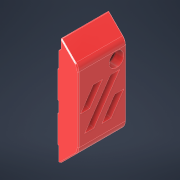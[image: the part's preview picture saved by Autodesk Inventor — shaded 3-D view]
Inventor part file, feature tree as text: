
AUTODESK INVENTOR PART (.ipt)
format: ipt  version: 2022.1 (Build 261234000, 234)  size: 578,560 bytes
history: native  units: mm
features: extrude x9, sketch x8, chamfer x7, projected_geometry x6, plane x3, reference x3, other x3, direct_edit x2, fillet x2, move_body x2, delete_face x1, hole x1
ambient origin geometry x8: Origin, YZ Plane, XZ Plane, XY Plane, X Axis, Y Axis, Z Axis, Center Point
bodies: Volumenkörper1 (feature_tree)
feature tree (47):
  extrude  "Extrusion1"  Depth=6.4mm
  plane  "Arbeitsebene1"
  extrude  "Extrusion2"  Depth=6.4mm
  chamfer  "Fase1"  Distance=6.4mm
  extrude  "Extrusion3"  Depth=10.0mm
  direct_edit  "Direktbearbeitung1"
  plane  "Arbeitsebene3"
  extrude  "Extrusion4"  Depth=10.0mm
  plane  "Arbeitsebene2"
  extrude  "Extrusion5"  Depth=10.0mm
  delete_face  "Fläche löschen1"
  extrude  "Extrusion7"  Depth=10.0mm TaperAngle=0.0deg
  extrude  "Extrusion8"  Depth=10.0mm
  chamfer  "Fase5"  Distance=7.9mm
  chamfer  "Fase6"  Distance=7.0mm Angle=45.0deg
  extrude  "Extrusion11"  TaperAngle=45.0deg  [1 undecoded]
  sketch  "Skizze13"  dims[d9=6.4mm d10=6.4mm d11=5.0mm d12=5.0mm d13=0.1mm d14=0.4mm d15=0.0mm d16=0.1mm d17=7.9mm d18=0.0mm d19=7.0mm d20=2.0mm d21=45.0deg d22=45.0deg d23=0.05mm d24=45.0deg d25=0.05mm d26=0.4mm d27=8.0mm d28=0.0mm d29=0.0mm d30=0.0mm d31=0.2mm d97=25.438174mm d99=3.8mm d102=3.304348mm d103=9.5mm d104=19.0mm d106=0.0mm d110=3.8mm d111=19.0mm d113=3.8mm d114=9.5mm d118=0.0mm d119=3.304348mm d124=15.705205mm d125=18.008696mm d126=25.215728mm d127=20.0mm d129=0.995652mm d130=1.0mm d131=0.0mm d146=20.0mm d147=10.0mm d148=12.607864mm d149=5.6mm d153=6.1mm d154=7.397555mm d155=2.198777mm d156=4.05mm d157=3.5mm d158=0.0mm d159=2.0mm d167=0.0mm d168=0.4mm d169=0.0mm d170=0.0mm d172=0.01mm d173=0.05mm d175=0.05mm d176=4.95mm d177=0.0mm d178=1.99mm d179=2.0mm d180=45.0deg d200=1.0mm d201=2.0mm d202=45.0deg d203=0.0mm d204=0.0mm d205=0.42mm d206=0.0mm d207=0.4mm d208=0.1mm d209=20.0mm d210=0.42mm d211=2.0mm d212=45.0deg d213=6.1mm d214=6.0mm d215=4.0mm d216=2.0mm d217=90.0deg d218=3.2mm d219=0.0mm d220=0.2mm d221=2.0mm d222=45.0deg d226=0.2mm d227=2.0mm d228=45.0deg d229=4.0mm d233=0.4mm d234=2.0mm d235=45.0deg d236=0.0mm d237=0.0mm d238=-0.5mm d171=0.872665mm]
  extrude  "Extrusion12"  Depth=10.0mm
  fillet  "Rundung7"  [1 undecoded]
  chamfer  "Fase7"  Distance=0.05mm
  hole  "Bohrung2"  [1 undecoded]
  chamfer  "Fase8"  Distance=8.0mm
  chamfer  "Fase10"  Distance=0.2mm
  fillet  "Rundung8"  Radius=25.438174mm
  chamfer  "Fase12"  Distance=3.8mm
  direct_edit  "Direktbearbeitung2"
  sketch  "Skizze1"  dims[d0=3.25mm d1=6.4mm]
  reference  "Referenz1"
  sketch  "Skizze2"  dims[d2=6.4mm d3=6.4mm]
  reference  "Referenz2"
  sketch  "Skizze3"  dims[d4=6.4mm]
  projected_geometry  "Projizierte Kontur1"
  sketch  "Skizze6"  dims[d5=6.4mm]
  sketch  "Skizze8"  dims[d6=5.0mm]
  reference  "Referenz13"
  sketch  "Skizze9"  dims[d7=5.0mm]
  sketch  "Skizze12"  dims[d8=6.4mm]
  projected_geometry  "Projizierte Kontur3"
  projected_geometry  "Projizierte Kontur4"
  projected_geometry  "Projizierte Kontur5"
  projected_geometry  "Projizierte Kontur6"
  projected_geometry  "Projizierte Kontur7"
  other  "<userpath>\Desktop\Voron-2-2.4r1\Custom\Misumi GE5C\Gruppe.iam"
  other  "Gruppe.iam"
  other  "Z-Joint-Normal:1"
  move_body  "Verschieben1"
  move_body  "Verschieben2"
note: 3 required parameter values undecoded (feature->parameter linkage not recoverable at this tier; creation-order binding heuristic only, values carry confidence <= 0.55)
